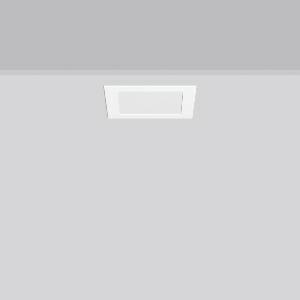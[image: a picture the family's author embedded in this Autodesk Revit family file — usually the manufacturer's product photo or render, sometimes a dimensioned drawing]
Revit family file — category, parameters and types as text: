
# Revit family: toledo_flat_square_e_672242_002_e096
name_source: partatom
category: Lighting Fixtures
units: mm (PartAtom-declared; Revit-internal decimal feet)

## family parameters
Cut with Voids When Loaded = No
Host = Face
Light Source = No
Part Type = Normal
Room Calculation Point = No
Round Connector Dimension = Use Diameter
Shared = No

## types (1)
- TOLEDO FLAT square E (1 x LED Modul 830, 730 lm, 3000)
    Apparent Load = 8 VA
    CIE Flux Codes = 49 80 96 100 100
    Color Rendering = 80
    Color Temperature = 3000
    Default Elevation = 1800 mm
    Description = Series: TOLEDO FLAT square
Square recessed downlight. For escape route illumination. Housing: die-cast aluminium, powder-coated. Lightguide and diffuser made of non-yellowing plastic (PMMA). Diffuser opal matt plastic. Ceiling installation with spring system. Including separate LED converter with connecting cable 250 mm. Suitable for connection to central battery systems. External driver with simple plug-in locking system. 
Colour: white
Length: 172 mm
Width: 172 mm
Height: 3 mm
Cut-out length: 156 mm
Cut-out width: 156 mm
Recess height: 35 mm
Luminaire: recess height: 31-51 mm
Weight: 423 g
Operating mode: maintained power mode
Lamp: LED
Socket: without socket
Colour temperature: 3000K
Colour rendering index (CRI): 80
System power: 8 W
Rated luminous flux: 730 lm
Luminous flux, emergency: 730 lm
System power, emergency: 8 W
Control gear: Regulated power supply
Protection class: II
Type of protection: IP 54
    Height = 0 mm  [stored 0 ft]
    Lamp = 1 x LED Modul 830
    Lamp Light Flux = 730 lm
    Lamp count = 1
    Length = 172 mm
    Lifetime = 50000 h
    Luminous efficacy = 91 lm/W
    Manufacturer = RZB
    ModVariant = No
    Model = 672242.002
    Mounting Place = Ceiling
    Mounting Type = Recessed
    Number of Poles = 1
    OnlyDefault = Yes
    Power Factor = 1
    Product Name = TOLEDO FLAT square E
    Product group = Recessed downlights
    ProductGroupID = 402
    Protection Class = Protection class II
    Protection Degree = IP 40
    RLX_Detail_Level = 1
    RLX_Emergency_Light_Flux = 730 lm
    RLX_Emergency_Type = 3
    RLX_Emergency_Type_DB = Yes
    RlxData = <blob elided: 9985 chars, md5=522f5e33>
    Socket = socket
    Standby Power = 0 W
    System Light Flux = 730 lm
    System Power = 8 W
    Type Comments = Product without accessories
    Type Image = 901486.002.jpg
    URL = http://relux.com
    VarID = ---
    Voltage = 230 V
    Voltage Range = 220-240 V
    Weight = 0.00 kg
    Width = 172 mm

note: [stored X ft] marks values corroborated as IEEE doubles in the binary element streams (Revit-internal decimal feet)

## geometry (parser evidence)
native form markers: Sweep x10
no freeform markers — native parametric forms only
